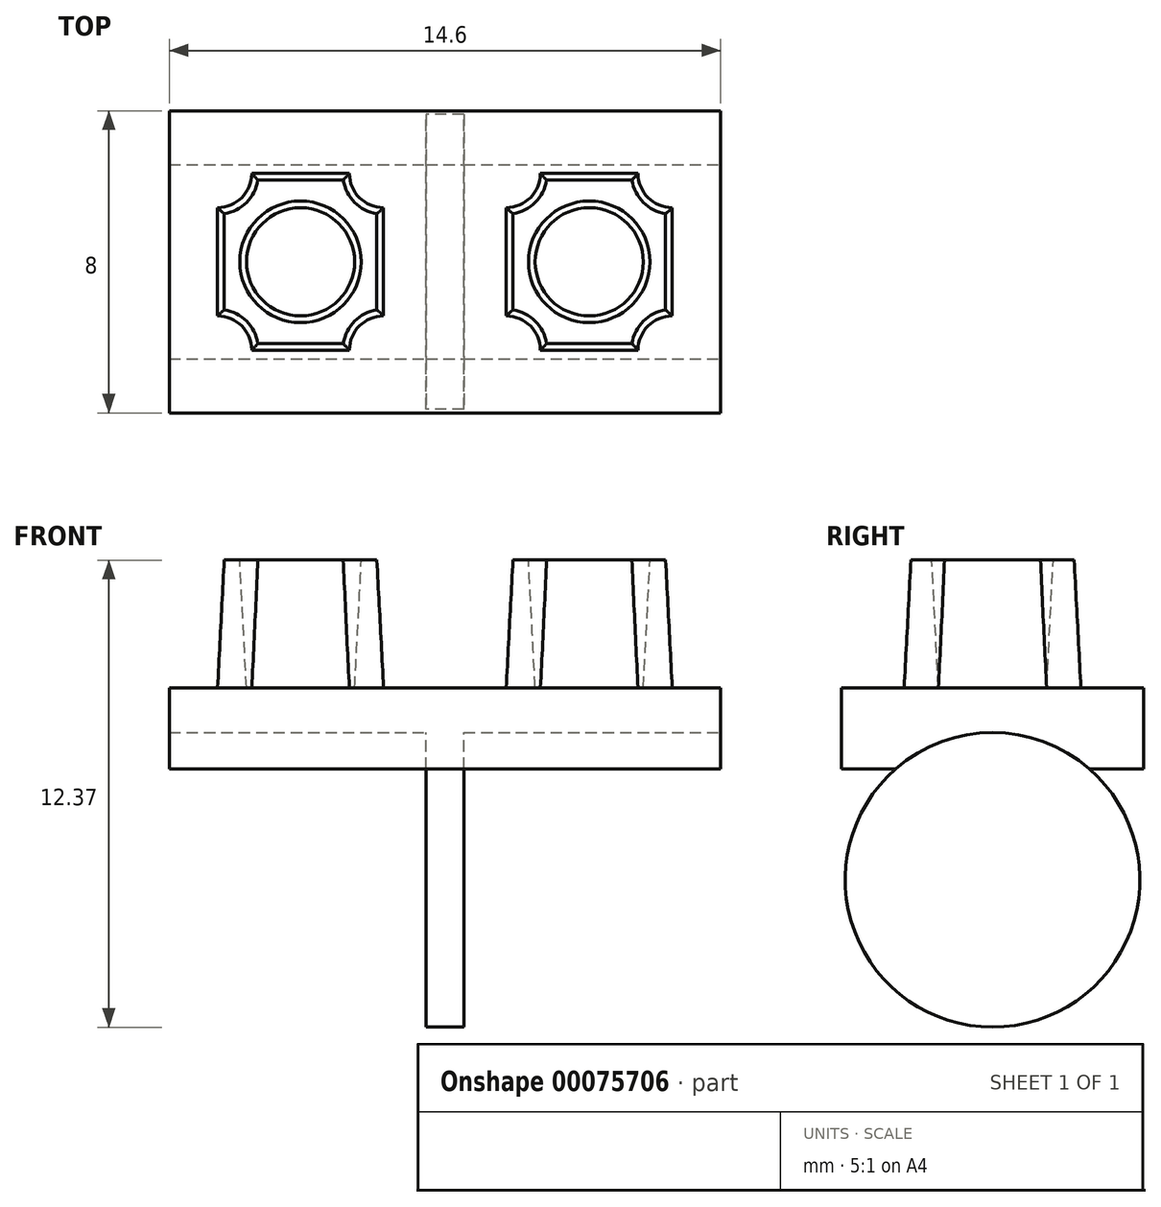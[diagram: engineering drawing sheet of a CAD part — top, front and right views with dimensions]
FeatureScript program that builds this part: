
annotation { "Feature Type Name" : "Feature", "Feature Type Description" : "" }
export const myFeature = defineFeature(function(context is Context, id is Id, definition is map)
    precondition{}
    {
        {
            var Q0;
            Q0=qCreatedBy(makeId("Front.planeOp"),FACE);
            var sketch = newSketch(context, id + "F0", { "sketchPlane" : qUnion([Q0])});
            skLineSegment(sketch, "E0", {"start": v(7.3, 0) * mm, "end": v(7.3, 2.15) * mm});
            skLineSegment(sketch, "E1", {"start": v(7.3, 2.15) * mm, "end": v(0, 2.15) * mm});
            skLineSegment(sketch, "E2", {"start": v(-7.3, 0) * mm, "end": v(7.3, 0) * mm});
            skLineSegment(sketch, "E3", {"start": v(-7.3, 0) * mm, "end": v(-7.3, 2.15) * mm});
            skLineSegment(sketch, "E4", {"start": v(-7.3, 2.15) * mm, "end": v(0, 2.15) * mm});
            skSolve(sketch);
        }
        {
            var Q0;
            Q0=makeQuery(id+"F0.imprint","IMPRINT",FACE,{"disambiguationData":[TD([[makeQuery(id+"F0.imprint","IMPRINT",EDGE,{"derivedFrom":sQuery(id+"F0.wireOp",EDGE,"E0")}),1.0]])]});
            extrude(context, id + "F1", {"entities" : qUnion([Q0]), "endBound" : BoundingType.SYMMETRIC, "depth" : 8 * mm});
        }
        {
            var Q0;
            Q0=qCreatedBy(makeId("Right.planeOp"),FACE);
            var sketch = newSketch(context, id + "F2", { "sketchPlane" : qUnion([Q0])});
            skCircle(sketch, "E5", {"center": v(0, -2.94) * mm, "radius": 3.9 * mm});
            skSolve(sketch);
        }
        {
            var Q0;
            Q0=makeQuery(id+"F2.imprint","IMPRINT",FACE,{"disambiguationData":[TD([[makeQuery(id+"F2.imprint","IMPRINT",EDGE,{"derivedFrom":sQuery(id+"F2.wireOp",EDGE,"E5")}),1.0]])]});
            extrude(context, id + "F3", {"entities" : qUnion([Q0]), "operationType" : NewBodyOperationType.REMOVE, "endBound" : BoundingType.THROUGH_ALL, "oppositeDirection" : true, "depth" : 25 * mm, "hasSecondDirection" : true, "secondDirectionBound" : SecondDirectionBoundingType.THROUGH_ALL, "secondDirectionOppositeDirection" : false, "secondDirectionDepth" : 25 * mm});
        }
        {
            var Q0;
            Q0=makeQuery(id+"F2.imprint","IMPRINT",FACE,{"disambiguationData":[TD([[makeQuery(id+"F2.imprint","IMPRINT",EDGE,{"derivedFrom":sQuery(id+"F2.wireOp",EDGE,"E5")}),1.0]])]});
            extrude(context, id + "F4", {"entities" : qUnion([Q0]), "operationType" : NewBodyOperationType.ADD, "endBound" : BoundingType.SYMMETRIC, "depth" : 1 * mm});
        }
        {
            var Q0;
            Q0=makeQuery(id+"F1.opExtrude","SWEPT_FACE",FACE,{"disambiguationData":[OSD([sQuery(id+"F0.wireOp",EDGE,"E1"),sQuery(id+"F0.wireOp",EDGE,"E4")])]});
            var sketch = newSketch(context, id + "F5", { "sketchPlane" : qUnion([Q0])});
            skCircle(sketch, "E6", {"center": v(-3.82, 0) * mm, "radius": 1.43 * mm});
            skCircle(sketch, "E7", {"center": v(3.63, 0) * mm, "radius": 1.46 * mm});
            skLineSegment(sketch, "E8.bottom", {"start": v(-6.02, -2.34) * mm, "end": v(-1.62, -2.34) * mm});
            skLineSegment(sketch, "E8.top", {"start": v(-6.02, 2.34) * mm, "end": v(-1.62, 2.34) * mm});
            skLineSegment(sketch, "E8.left", {"start": v(-6.02, -2.34) * mm, "end": v(-6.02, 2.34) * mm});
            skLineSegment(sketch, "E8.right", {"start": v(-1.62, -2.34) * mm, "end": v(-1.62, 2.34) * mm});
            skCircle(sketch, "E9", {"center": v(-1.62, 2.34) * mm, "radius": 0.9 * mm});
            skCircle(sketch, "E10", {"center": v(-6.02, 2.34) * mm, "radius": 0.9 * mm});
            skCircle(sketch, "E11", {"center": v(-6.02, -2.34) * mm, "radius": 0.9 * mm});
            skCircle(sketch, "E12", {"center": v(-1.62, -2.34) * mm, "radius": 0.9 * mm});
            skSolve(sketch);
        }
        {
            var Q0;
            Q0=makeQuery(id+"F5.imprint","IMPRINT",FACE,{"disambiguationData":[TD([[makeQuery(id+"F5.imprint","IMPRINT",EDGE,{"derivedFrom":sQuery(id+"F5.wireOp",EDGE,"E6")}),-1.0]])]});
            extrude(context, id + "F6", {"entities" : qUnion([Q0]), "operationType" : NewBodyOperationType.ADD, "depth" : 3.38 * mm, "hasDraft" : true, "draftAngle" : 3 * degree, "draftPullDirection" : true});
        }
        {
            var Q0;
            Q0=makeQuery(id+"F1.opExtrude","SWEPT_BODY",BODY,{"disambiguationData":[OSD([sQuery(id+"F0.wireOp",EDGE,"E0"),sQuery(id+"F0.wireOp",EDGE,"E1"),sQuery(id+"F0.wireOp",EDGE,"E2"),sQuery(id+"F0.wireOp",EDGE,"E3"),sQuery(id+"F0.wireOp",EDGE,"E4")])]});
            var Q1;
            Q1=qCreatedBy(makeId("Right.planeOp"),FACE);
            mirror(context, id + "F7", {"operationType" : NewBodyOperationType.ADD, "entities" : qUnion([Q0]), "mirrorPlane" : qUnion([Q1])});
        }
    });
